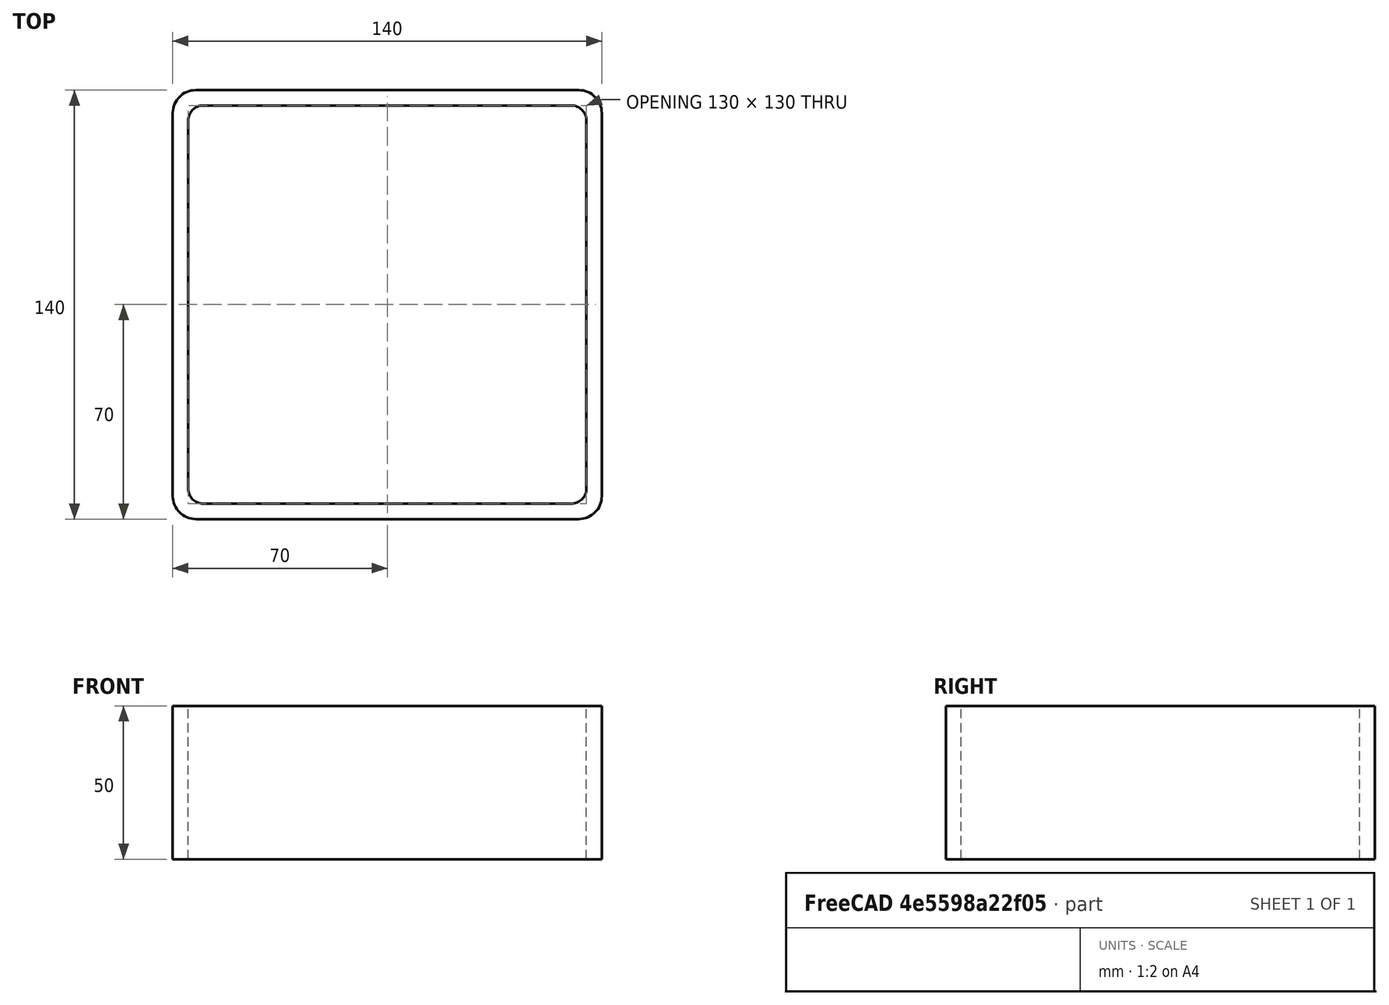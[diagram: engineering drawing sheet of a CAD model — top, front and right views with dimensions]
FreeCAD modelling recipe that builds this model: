
FCSTD DOCUMENT  (FreeCAD 0.15R4671 (Git))
Label: Square hollow section 140x140x5 EN10219 S235JRH
License: All rights reserved
LicenseURL: http://en.wikipedia.org/wiki/All_rights_reserved
objects: Sketcher::SketchObject×1, Part::Extrusion×1
note: 2 computed .brp shape members not serialized (recipe doc carries the construction recipe); baked Part::Feature solids carry a one-line shape summary decoded from their .brp

FEATURE [Sketcher::SketchObject] Sketch
  sketch-geometry (16):
    g0: LineSegment StartX=-60 StartY=65 StartZ=0 EndX=60 EndY=65 EndZ=0
    g1: LineSegment StartX=65 StartY=60 StartZ=0 EndX=65 EndY=-60 EndZ=0
    g2: LineSegment StartX=60 StartY=-65 StartZ=0 EndX=-60 EndY=-65 EndZ=0
    g3: LineSegment StartX=-65 StartY=-60 StartZ=0 EndX=-65 EndY=60 EndZ=0
    g4: LineSegment StartX=-62.5 StartY=70 StartZ=0 EndX=62.5 EndY=70 EndZ=0
    g5: LineSegment StartX=70 StartY=62.5 StartZ=0 EndX=70 EndY=-62.5 EndZ=0
    g6: LineSegment StartX=62.5 StartY=-70 StartZ=0 EndX=-62.5 EndY=-70 EndZ=0
    g7: LineSegment StartX=-70 StartY=-62.5 StartZ=0 EndX=-70 EndY=62.5 EndZ=0
    g8: ArcOfCircle CenterX=-60 CenterY=60 CenterZ=0 NormalX=0 NormalY=0 NormalZ=1 Radius=5 StartAngle=1.5708 EndAngle=3.14159
    g9: ArcOfCircle CenterX=60 CenterY=60 CenterZ=0 NormalX=0 NormalY=0 NormalZ=1 Radius=5 StartAngle=0 EndAngle=1.5708
    g10: ArcOfCircle CenterX=60 CenterY=-60 CenterZ=0 NormalX=0 NormalY=0 NormalZ=1 Radius=5 StartAngle=4.71239 EndAngle=6.28319
    g11: ArcOfCircle CenterX=-60 CenterY=-60 CenterZ=0 NormalX=0 NormalY=0 NormalZ=1 Radius=5 StartAngle=3.14159 EndAngle=4.71239
    g12: ArcOfCircle CenterX=62.5 CenterY=62.5 CenterZ=0 NormalX=0 NormalY=0 NormalZ=1 Radius=7.5 StartAngle=0 EndAngle=1.5708
    g13: ArcOfCircle CenterX=62.5 CenterY=-62.5 CenterZ=0 NormalX=0 NormalY=0 NormalZ=1 Radius=7.5 StartAngle=4.71239 EndAngle=6.28319
    g14: ArcOfCircle CenterX=-62.5 CenterY=-62.5 CenterZ=0 NormalX=0 NormalY=0 NormalZ=1 Radius=7.5 StartAngle=3.14159 EndAngle=4.71239
    g15: ArcOfCircle CenterX=-62.5 CenterY=62.5 CenterZ=0 NormalX=0 NormalY=0 NormalZ=1 Radius=7.5 StartAngle=1.5708 EndAngle=3.14159
  constraints (36):
    c: Horizontal(g2)
    c: Vertical(g3)
    c: Horizontal(g6)
    c: Vertical(g7)
    c: Tangent(g3,g8) = 1.5708
    c: Tangent(g0,g8) = 1.5708
    c: Tangent(g0,g9) = 1.5708
    c: Tangent(g1,g9) = 1.5708
    c: Tangent(g1,g10) = 1.5708
    c: Tangent(g2,g10) = 1.5708
    c: Tangent(g2,g11) = 1.5708
    c: Tangent(g3,g11) = 1.5708
    c: Tangent(g4,g12) = 1.5708
    c: Tangent(g5,g12) = 1.5708
    c: Tangent(g5,g13) = 1.5708
    c: Tangent(g6,g13) = 1.5708
    c: Tangent(g6,g14) = 1.5708
    c: Tangent(g7,g14) = 1.5708
    c: Tangent(g7,g15) = 1.5708
    c: Tangent(g4,g15) = 1.5708
    c: Equal(g9,g8)
    c: Equal(g9,g11)
    c: Equal(g9,g10)
    c: Equal(g12,g15)
    c: Equal(g12,g14)
    c: Equal(g12,g13)
    c: Symmetric(g4,g6,g-1)
    c: Symmetric(g7,g5,g-2)
    c: DistanceY(g4,g6) = -140
    c: DistanceX(g7,g5) = 140
    c: Symmetric(g3,g1,g-2)
    c: Symmetric(g0,g2,g-1)
    c: DistanceY(g0,g4) = 5
    c: DistanceX(g5,g1) = -5
    c: Radius(g9) = 5
    c: Radius(g12) = 7.5
FEATURE [Part::Extrusion] Extrude  label="Square hollow section 140x140x5 EN10219 S235JRH"
  Base = -> Sketch
  Dir = (0,0,50)
  Solid = true
